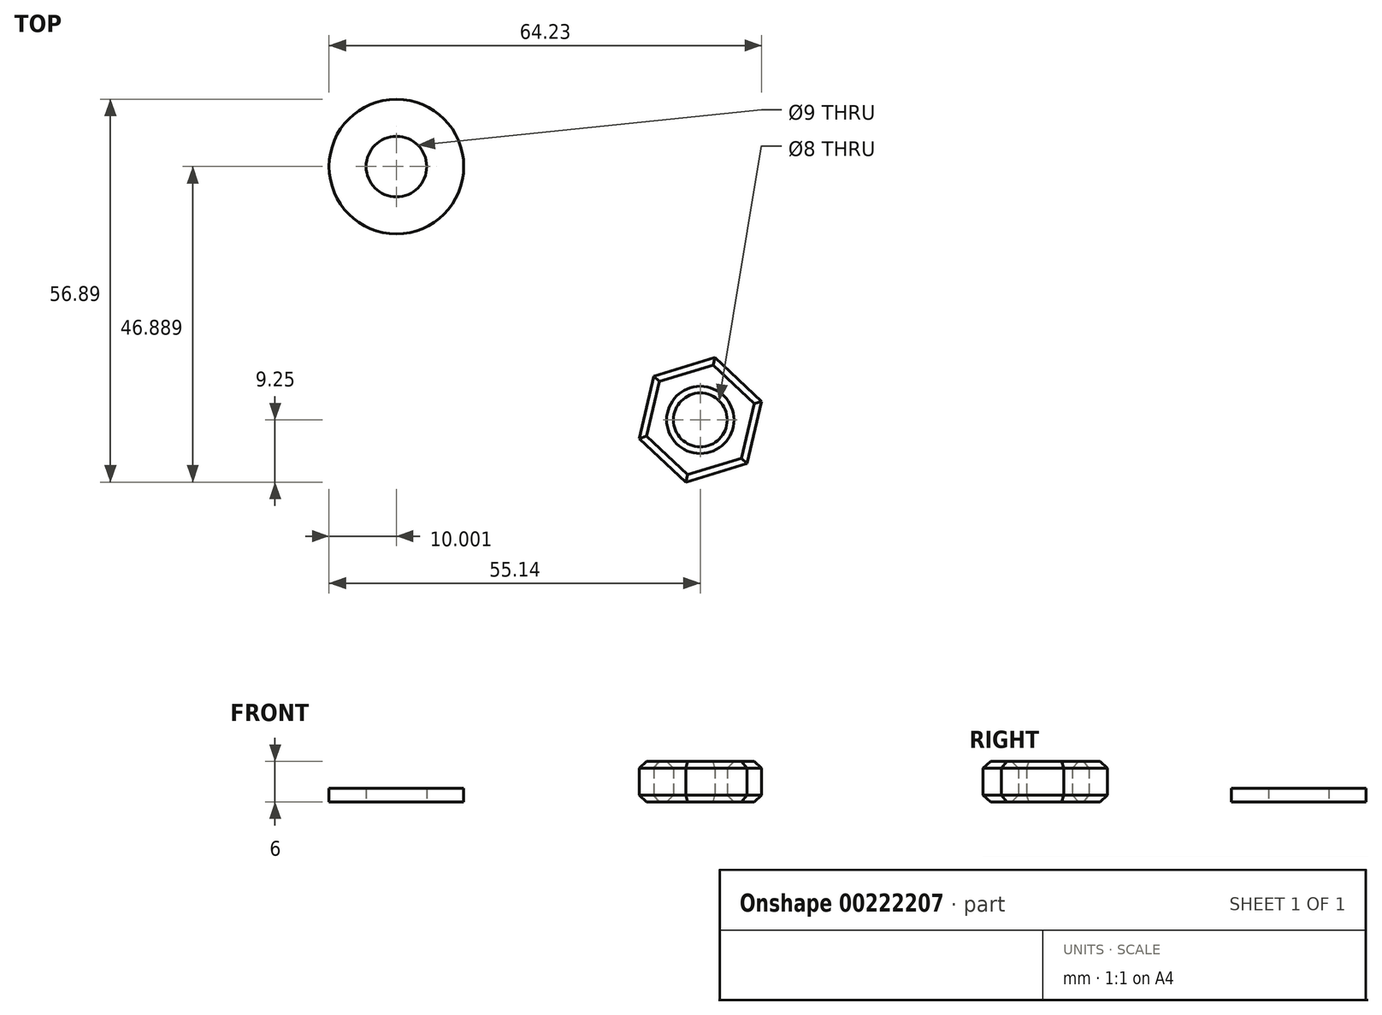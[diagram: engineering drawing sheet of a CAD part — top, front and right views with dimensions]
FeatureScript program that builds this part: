
annotation { "Feature Type Name" : "Feature", "Feature Type Description" : "" }
export const myFeature = defineFeature(function(context is Context, id is Id, definition is map)
    precondition{}
    {
        {
            var Q0;
            Q0=qCreatedBy(makeId("Top.planeOp"),FACE);
            var sketch = newSketch(context, id + "F0", { "sketchPlane" : qUnion([Q0])});
            skCircle(sketch, "E0.cCircle", {"center": v(0, 0) * mm, "radius": 9.5 * mm, "construction": true});
            skLineSegment(sketch, "E0.0", {"start": v(9.1, 2.76) * mm, "end": v(6.93, -6.5) * mm});
            skLineSegment(sketch, "E0.1", {"start": v(6.93, -6.5) * mm, "end": v(-2.16, -9.25) * mm});
            skLineSegment(sketch, "E0.2", {"start": v(-2.16, -9.25) * mm, "end": v(-9.1, -2.76) * mm});
            skLineSegment(sketch, "E0.3", {"start": v(-9.1, -2.76) * mm, "end": v(-6.93, 6.5) * mm});
            skLineSegment(sketch, "E0.4", {"start": v(-6.93, 6.5) * mm, "end": v(2.16, 9.25) * mm});
            skLineSegment(sketch, "E0.5", {"start": v(2.16, 9.25) * mm, "end": v(9.1, 2.76) * mm});
            skCircle(sketch, "E1", {"center": v(0, 0) * mm, "radius": 4 * mm});
            skSolve(sketch);
        }
        {
            var Q0;
            Q0=makeQuery(id+"F0.imprint","IMPRINT",FACE,{"disambiguationData":[TD([[makeQuery(id+"F0.imprint","IMPRINT",EDGE,{"derivedFrom":sQuery(id+"F0.wireOp",EDGE,"E0.0")}),-1.0]])]});
            extrude(context, id + "F1", {"entities" : qUnion([Q0]), "depth" : 6 * mm});
        }
        {
            var Q0;
            Q0=makeQuery(id+"F1.opExtrude","CAP_EDGE",EDGE,{"disambiguationData":[OSD([sQuery(id+"F0.wireOp",EDGE,"E0.3")])],"isStart":false});
            var Q1;
            Q1=makeQuery(id+"F1.opExtrude","CAP_EDGE",EDGE,{"disambiguationData":[OSD([sQuery(id+"F0.wireOp",EDGE,"E0.2")])],"isStart":false});
            var Q2;
            Q2=makeQuery(id+"F1.opExtrude","CAP_EDGE",EDGE,{"disambiguationData":[OSD([sQuery(id+"F0.wireOp",EDGE,"E0.1")])],"isStart":false});
            var Q3;
            Q3=makeQuery(id+"F1.opExtrude","CAP_EDGE",EDGE,{"disambiguationData":[OSD([sQuery(id+"F0.wireOp",EDGE,"E0.0")])],"isStart":false});
            var Q4;
            Q4=makeQuery(id+"F1.opExtrude","CAP_EDGE",EDGE,{"disambiguationData":[OSD([sQuery(id+"F0.wireOp",EDGE,"E0.5")])],"isStart":false});
            var Q5;
            Q5=makeQuery(id+"F1.opExtrude","CAP_EDGE",EDGE,{"disambiguationData":[OSD([sQuery(id+"F0.wireOp",EDGE,"E0.4")])],"isStart":false});
            var Q6;
            Q6=makeQuery(id+"F1.opExtrude","CAP_FACE",FACE,{"disambiguationData":[OSD([sQuery(id+"F0.wireOp",EDGE,"E0.0"),sQuery(id+"F0.wireOp",EDGE,"E0.1"),sQuery(id+"F0.wireOp",EDGE,"E0.2"),sQuery(id+"F0.wireOp",EDGE,"E0.3"),sQuery(id+"F0.wireOp",EDGE,"E0.4"),sQuery(id+"F0.wireOp",EDGE,"E0.5"),sQuery(id+"F0.wireOp",EDGE,"E1")])],"isStart":true});
            var Q7;
            Q7=makeQuery(id+"F1.opExtrude","SWEPT_FACE",FACE,{"disambiguationData":[OSD([sQuery(id+"F0.wireOp",EDGE,"E1")])]});
            chamfer(context, id + "F2", {"entities" : qUnion([Q0, Q1, Q2, Q3, Q4, Q5, Q6, Q7]), "width" : 1 * mm, "tangentPropagation" : true});
        }
        {
            var Q0;
            Q0=qCreatedBy(makeId("Top.planeOp"),FACE);
            var sketch = newSketch(context, id + "F3", { "sketchPlane" : qUnion([Q0])});
            skCircle(sketch, "E2", {"center": v(-45.14, 37.64) * mm, "radius": 4.5 * mm});
            skCircle(sketch, "E3", {"center": v(-45.14, 37.64) * mm, "radius": 10 * mm});
            skSolve(sketch);
        }
        {
            var Q0;
            Q0=makeQuery(id+"F3.imprint","IMPRINT",FACE,{"disambiguationData":[TD([[makeQuery(id+"F3.imprint","IMPRINT",EDGE,{"derivedFrom":sQuery(id+"F3.wireOp",EDGE,"E2")}),-1.0]])]});
            extrude(context, id + "F4", {"entities" : qUnion([Q0]), "depth" : 2 * mm});
        }
    });
